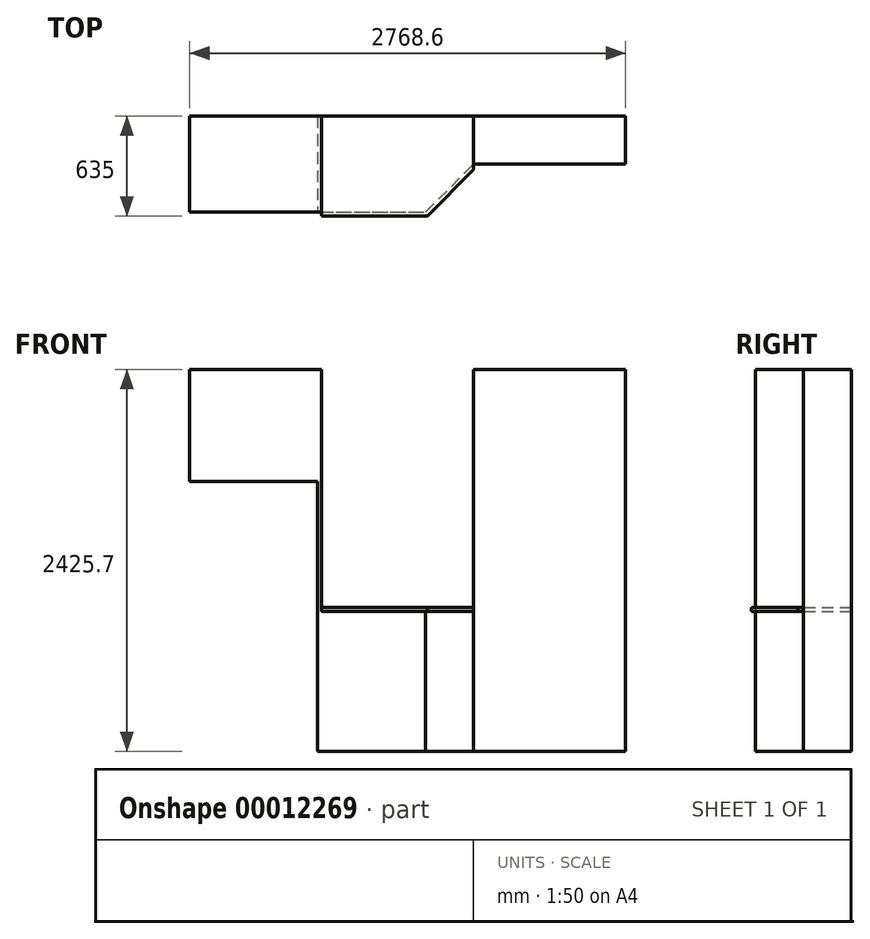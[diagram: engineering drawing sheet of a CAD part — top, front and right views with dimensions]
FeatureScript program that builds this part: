
annotation { "Feature Type Name" : "Feature", "Feature Type Description" : "" }
export const myFeature = defineFeature(function(context is Context, id is Id, definition is map)
    precondition{}
    {
        {
            var Q0;
            Q0=qCreatedBy(makeId("Top.planeOp"),FACE);
            cPlane(context, id + "F0", {"entities" : qUnion([Q0]), "cplaneType" : CPlaneType.OFFSET, "offset" : 2425.7 * mm, "width" : 152.4 * mm, "height" : 152.4 * mm});
        }
        {
            var Q0;
            Q0=qCreatedBy(makeId("Top.planeOp"),FACE);
            cPlane(context, id + "F1", {"entities" : qUnion([Q0]), "cplaneType" : CPlaneType.OFFSET, "offset" : 889 * mm, "width" : 152.4 * mm, "height" : 152.4 * mm});
        }
        {
            var Q0;
            Q0=qCreatedBy(id+"F0.planeOp",FACE);
            cPlane(context, id + "F2", {"entities" : qUnion([Q0]), "cplaneType" : CPlaneType.OFFSET, "offset" : 711.2 * mm, "oppositeDirection" : true, "width" : 152.4 * mm, "height" : 152.4 * mm});
        }
        {
            var Q0;
            Q0=qCreatedBy(id+"F1.planeOp",FACE);
            cPlane(context, id + "F3", {"entities" : qUnion([Q0]), "cplaneType" : CPlaneType.OFFSET, "offset" : 25.4 * mm, "width" : 152.4 * mm, "height" : 152.4 * mm});
        }
        {
            var Q0;
            Q0=qCreatedBy(makeId("Top.planeOp"),FACE);
            var sketch = newSketch(context, id + "F4", { "sketchPlane" : qUnion([Q0])});
            skLineSegment(sketch, "E0.bottom", {"start": v(0, 0) * mm, "end": v(2768.6, 0) * mm});
            skLineSegment(sketch, "E0.top", {"start": v(0, -609.6) * mm, "end": v(838.2, -609.6) * mm});
            skLineSegment(sketch, "E0.left", {"start": v(0, 0) * mm, "end": v(0, -609.6) * mm});
            skLineSegment(sketch, "E1.left", {"start": v(812.8, 0) * mm, "end": v(812.8, -609.6) * mm});
            skLineSegment(sketch, "E1.right", {"start": v(838.2, 0) * mm, "end": v(838.2, -609.6) * mm});
            skLineSegment(sketch, "E2", {"start": v(838.2, -609.6) * mm, "end": v(838.2, -609.6) * mm});
            skLineSegment(sketch, "E3", {"start": v(838.2, -609.6) * mm, "end": v(1498.6, -609.6) * mm});
            skLineSegment(sketch, "E4", {"start": v(1498.6, -609.6) * mm, "end": v(1803.4, -304.8) * mm});
            skLineSegment(sketch, "E5", {"start": v(1803.4, -340.72) * mm, "end": v(1803.4, 0) * mm});
            skLineSegment(sketch, "E6", {"start": v(1803.4, -304.8) * mm, "end": v(2768.6, -304.8) * mm});
            skLineSegment(sketch, "E7", {"start": v(2768.6, -304.8) * mm, "end": v(2768.6, 0) * mm});
            skLineSegment(sketch, "E8", {"start": v(838.2, -609.6) * mm, "end": v(838.2, -635) * mm});
            skLineSegment(sketch, "E9", {"start": v(838.2, -635) * mm, "end": v(1509.12, -635) * mm});
            skLineSegment(sketch, "E10", {"start": v(1509.12, -635) * mm, "end": v(1803.4, -340.72) * mm});
            skSolve(sketch);
        }
        {
            var Q0;
            {var subQ1=sQuery(id+"F4.wireOp",EDGE,"E6");Q0=makeQuery(id+"F4.imprint","IMPRINT",FACE,{"disambiguationData":[TD([[makeQuery(id+"F4.imprint","IMPRINT",EDGE,{"derivedFrom":subQ1}),1.0]])]});}
            var Q1;
            Q1=qCreatedBy(id+"F0.planeOp",FACE);
            extrude(context, id + "F5", {"entities" : qUnion([Q0]), "endBound" : BoundingType.UP_TO_SURFACE, "endBoundEntityFace" : qUnion([Q1]), "depth" : 25.4 * mm});
        }
        {
            var Q0;
            {var subQ4=sQuery(id+"F4.wireOp",EDGE,"E1.right");Q0=makeQuery(id+"F4.imprint","IMPRINT",FACE,{"disambiguationData":[TD([[makeQuery(id+"F4.imprint","IMPRINT",EDGE,{"derivedFrom":subQ4}),1.0]])]});}
            var Q1;
            Q1=qCreatedBy(id+"F1.planeOp",FACE);
            extrude(context, id + "F6", {"entities" : qUnion([Q0]), "operationType" : NewBodyOperationType.ADD, "endBound" : BoundingType.UP_TO_SURFACE, "endBoundEntityFace" : qUnion([Q1]), "depth" : 25.4 * mm});
        }
        {
            var Q0;
            {var subQ1=sQuery(id+"F4.wireOp",EDGE,"E1.left");Q0=makeQuery(id+"F4.imprint","IMPRINT",FACE,{"disambiguationData":[TD([[makeQuery(id+"F4.imprint","IMPRINT",EDGE,{"derivedFrom":subQ1}),1.0]])]});}
            var Q1;
            Q1=qCreatedBy(id+"F0.planeOp",FACE);
            extrude(context, id + "F7", {"entities" : qUnion([Q0]), "operationType" : NewBodyOperationType.ADD, "endBound" : BoundingType.UP_TO_SURFACE, "endBoundEntityFace" : qUnion([Q1]), "depth" : 25.4 * mm});
        }
        {
            var Q0;
            {var subQ0=sQuery(id+"F4.wireOp",EDGE,"E0.left");Q0=makeQuery(id+"F4.imprint","IMPRINT",FACE,{"disambiguationData":[TD([[makeQuery(id+"F4.imprint","IMPRINT",EDGE,{"derivedFrom":subQ0}),1.0]])]});}
            var Q1;
            Q1=qCreatedBy(id+"F0.planeOp",FACE);
            var Q2;
            Q2=qCreatedBy(id+"F2.planeOp",FACE);
            extrude(context, id + "F8", {"entities" : qUnion([Q0]), "operationType" : NewBodyOperationType.ADD, "endBound" : BoundingType.UP_TO_SURFACE, "endBoundEntityFace" : qUnion([Q1]), "depth" : 25.4 * mm, "hasSecondDirection" : true, "secondDirectionBound" : BoundingType.UP_TO_SURFACE, "secondDirectionOppositeDirection" : false, "secondDirectionBoundEntityFace" : qUnion([Q2]), "secondDirectionDepth" : 1778 * mm});
        }
        {
            var Q0;
            Q0=makeQuery(id+"F4.imprint","IMPRINT",FACE,{"disambiguationData":[TD([[makeQuery(id+"F4.imprint","IMPRINT",EDGE,{"derivedFrom":sQuery(id+"F4.wireOp",EDGE,"E3")}),-1.0]])]});
            var Q1;
            {var subQ4=sQuery(id+"F4.wireOp",EDGE,"E1.right");Q1=makeQuery(id+"F4.imprint","IMPRINT",FACE,{"disambiguationData":[TD([[makeQuery(id+"F4.imprint","IMPRINT",EDGE,{"derivedFrom":subQ4}),1.0]])]});}
            var Q2;
            Q2=qCreatedBy(id+"F3.planeOp",FACE);
            var Q3;
            Q3=qCreatedBy(id+"F1.planeOp",FACE);
            extrude(context, id + "F9", {"entities" : qUnion([Q0, Q1]), "endBound" : BoundingType.UP_TO_SURFACE, "endBoundEntityFace" : qUnion([Q2]), "depth" : 25.4 * mm, "hasSecondDirection" : true, "secondDirectionBound" : BoundingType.UP_TO_SURFACE, "secondDirectionOppositeDirection" : false, "secondDirectionBoundEntityFace" : qUnion([Q3]), "secondDirectionDepth" : 25.4 * mm});
        }
    });
